# Revit family: Faucet-Lavatory-American_Standard-Innsbrook_Selectronic-605B20X_Series
name_source: partatom
category: Plumbing Fixtures
units: mm (PartAtom-declared; Revit-internal decimal feet)

## family parameters
Always vertical = No
Cut with Voids When Loaded = No
OmniClass Number = 23.45.55.14
OmniClass Title = Single Faucets
Part Type = Normal
Room Calculation Point = No
Round Connector Dimension = Use Diameter
Shared = Yes
Work Plane-Based = Yes

## types (3) — shared parameters
605XTMV1070- Mixing Valve (Optional) = No
ADA Compliant = Yes
ANSI A117.1 = Yes
ASME A112.18.1/CSA B125.1 = Yes
Assembly Code = D2020300
CW Connection = No
CWFU = 1.5
Default Elevation = 0"
Finish = Brass-American Standard-002-Polished Chrome
Finish- Sensor = Plastic-American Standard-Black
HW Connection = No
HWFU = 1.5
Height = 5 1/8"
Height- Spout = 4 5/16"
Hole Width = 1 3/8"
Installation Type = Deck Mounted
Length = 6 7/8"
Manufacturer = American Standard
Material = Brass-American Standard-002-Polished Chrome
NSF 61/Section 9, NSF 372 = Yes
PK00.BBU- Battery Back-Up (Optional) = No
Power Kit- Optional PK00.CRP (Sold Separately) = No
Power Kit- Optional PK00.HAC (Sold Separately) = No
Power Kit- Optional PK00.MAC (Sold Separately) = No
Power Kit- Optional PK00.PAC (Sold Separately) = No
Power Kit- Optional PK00.WRK (Sold Separately) = No
Price = Prices may vary. Please consult Manufacturer Representative for most up-to-date price list.
Product Documentation Link = https://americanstandard.box.com
Product Page URL = https://www.americanstandard-us.com
Revised Date = 03/28/2022
Tempered Water Connection = Yes
Tempered Water Connection Diameter = 3/8"
Touchless, Water Efficient = Yes
URL = https://www.americanstandard-us.com
Vent Connection = No
WFU = 2
Warranty Information = 5 Year Limited Warranty
Waste Connection = No
Water Pressure = 20 to 125 psi
Width = 6 1/8"

## per-type parameters (varying)
| type | CEC Compliant | CalGreen Compliant | Description | EPA WaterSense® Certified | Flow Rate |
| 605B.205.002 | Yes | Yes | Innsbrook® Selectronic® Touchless Faucet, Base Model, 0.5 gpm/1.9 Lpm | No | 1 GPM |
| 605B.202.002 | No | No | Innsbrook® Selectronic® Touchless Faucet, Base Model, 1.5 gpm/5.7 Lpm | Yes | 2 GPM |
| 605B.204.002 | Yes | Yes | Innsbrook® Selectronic® Touchless Metering Faucet, Base Model, 0.35 gpm/1.3 Lpm | No | 0 GPM |

note: column(s) folded — value = type name in every type: Model

## geometry (parser evidence)
native form markers: Sweep x2
no freeform markers — native parametric forms only
